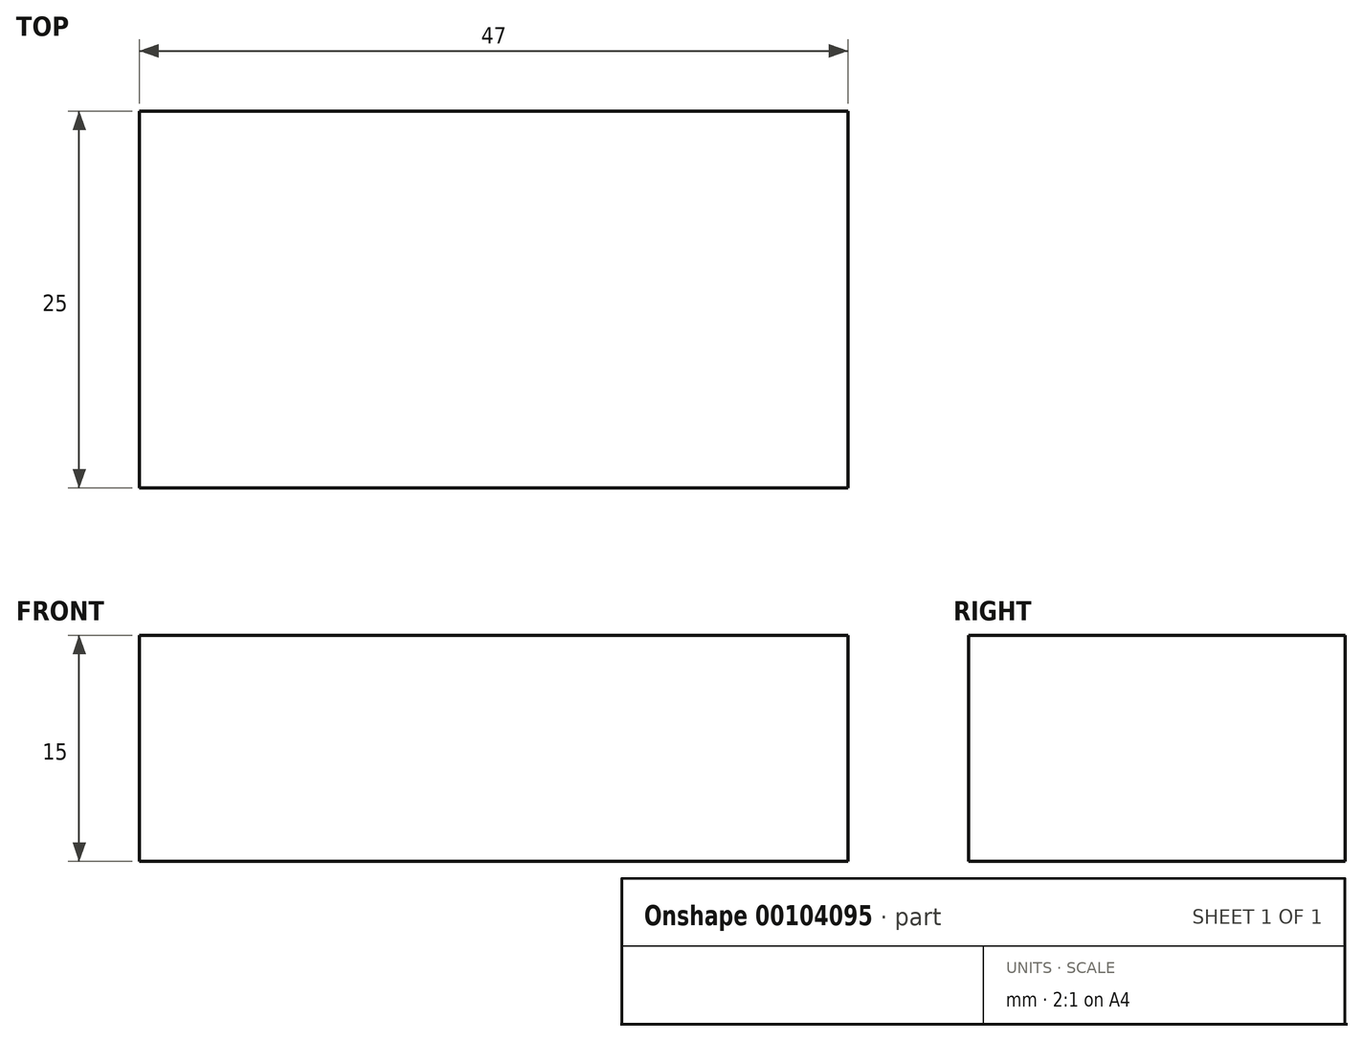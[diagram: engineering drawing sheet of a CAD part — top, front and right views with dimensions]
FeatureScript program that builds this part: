
annotation { "Feature Type Name" : "Feature", "Feature Type Description" : "" }
export const myFeature = defineFeature(function(context is Context, id is Id, definition is map)
    precondition{}
    {
        {
            var Q0;
            Q0=qCreatedBy(makeId("Front.planeOp"),FACE);
            var sketch = newSketch(context, id + "F0", { "sketchPlane" : qUnion([Q0])});
            skLineSegment(sketch, "E0.bottom", {"start": v(-13.76, 7.85) * mm, "end": v(33.24, 7.85) * mm});
            skLineSegment(sketch, "E0.top", {"start": v(-13.76, -7.15) * mm, "end": v(33.24, -7.15) * mm});
            skLineSegment(sketch, "E0.left", {"start": v(-13.76, 7.85) * mm, "end": v(-13.76, -7.15) * mm});
            skLineSegment(sketch, "E0.right", {"start": v(33.24, 7.85) * mm, "end": v(33.24, -7.15) * mm});
            skSolve(sketch);
        }
        {
            var Q0;
            Q0 = qSketchRegion(id + "F0", true);
            extrude(context, id + "F1", {"entities" : qUnion([Q0]), "depth" : 25 * mm});
        }
    });
